# Revit family: RAS_U2FVG_10-18_Indoor Unit
name_source: partatom
category: Mechanical Equipment
revit_build: Autodesk Revit 2017 (Build: 20160225_1515(x64)
units: mm (PartAtom-declared; Revit-internal decimal feet)

## family parameters
Always vertical = Yes
Cut with Voids When Loaded = No
OmniClass Number = 23.75.00.00
OmniClass Title = Climate Control (HVAC)
Part Type = Normal
Room Calculation Point = No
Round Connector Dimension = Use Diameter
Shared = No
Work Plane-Based = No

## types (3) — shared parameters
Article Description = R32 Console
Compressor-Motor Output W = -
Compressor-Type = -
Content Supplier URL = www.hcltech.com
Custom = Yes
Depth (mm) = 220 mm  [stored 0.721785 ft]
Description = R32 Console
Drain pipe(mm) = 16 mm  [stored 0.0524934 ft]
Duct diameters(mm) = -
EMCS = 4
ETIM Article Class = EC001213
Energy class-Cooling/Heating = A++ / A+
Frequency (Hz) = 50Hz
Height (mm) = 600 mm
Left Side Clearance (mm) (default) = 50 mm  [stored 0.164042 ft]
MCA (A) = -
MEPcontent Class = HEATPUMP
MOCP (A) = 15
Manufacturer = Toshiba
Manufacturer URL = https://www.toshiba-carrier.co.jp
Operating range degC-Cooling = 21 - 32
Operating range degC-Heating = 0 - 28
Piping diameter Liquid (mm) = 6 mm  [stored 0.019685 ft]
Product Line = TCTC
Red = Colour RGB-255 000 000
Refrigerant information = R410A
Revit Version = 2017
Right Side Clearance (mm) (default) = 50 mm  [stored 0.164042 ft]
Sound pressure dB(A)-Cooling/Heating-Low+ = -
Sound pressure dB(A)-Cooling/Heating-Mid+ = -
Static pressure = -
Top Clearance (mm) (default) = 70 mm  [stored 0.229659 ft]
URL = https://www.toshiba-carrier.co.jp
Voltage (V) = 220-240V
Weight (Kg) = 16
White = Colour RGB-255 255 255
Width (mm) = 700 mm  [stored 2.29659 ft]

## per-type parameters (varying)
| type | Airflow m3/h -Cooling/Heating | Pdesigh-Cooling/Heating | Piping diameter Gas (mm) | Power consumption-Cooling | Power consumption-Heating | Rated Capacity kW-Cooling/Heating | Rated Power Consumption kW-Cooling/Heating | Rated efficiency-EER / COP | Running current-Cooling | Running current-Heating | Seasonal Efficiency-SEER  / SCOP | Sound pressure dB(A)-Cooling/Heating- High | Sound pressure dB(A)-Cooling/Heating-Low | Sound pressure dB(A)-Cooling/Heating-Mid | Starting current |
| RAS-B10U2FVG-E1 | 468 / 510 | 2.5 / 2.5 (Tbiv= -7degC) | 10 mm  [stored 0.0328084 ft] | 20 | 25 | 2.5 / 3.2 | 0.60 / 0.86 | 4.17 / 3.72 | 0.17 - 0.15 | 0.20 - 0.19 | 6.6 / 4.2 | 39 / 39 | 26 / 26 | 32 / 32 | 4.50 - 3.00 |
| RAS-B13U2FVG-E1 | 510 / 552 | 3.5 / 3.0 (Tbiv= -7degC) | 10 mm  [stored 0.0328084 ft] | 25 | 30 | 3.5 / 4.2 | 1.10 / 1.25 | 3.18 / 3.36 | 0.20 - 0.18 | 0.24 - 0.22 | 6.4 / 4.2 | 40 / 40 | 27 / 27 | 33 / 33 | 5.95 - 5.15 |
| RAS-B18U2FVG-E1 | 600 / 642 | 5.0 / 4.0 (Tbiv= -7degC) | 13 mm | 35 | 40 | 5.0 / 6.2 | 1.75 / 2.00 | 2.86 / 2.93 | 0.27 - 0.24 | 0.30 - 0.28 | 6.2 / 4.0 | 45 / 46 | 34 / 34 | 40 / 40 | 9.50 - 7.55 |

note: column(s) folded — value = type name in every type: Article Type, Manufacturer Art. No., Model

note: [stored X ft] marks values corroborated as IEEE doubles in the binary element streams (Revit-internal decimal feet)

## geometry (parser evidence)
native form markers: Sweep x5
no freeform markers — native parametric forms only
